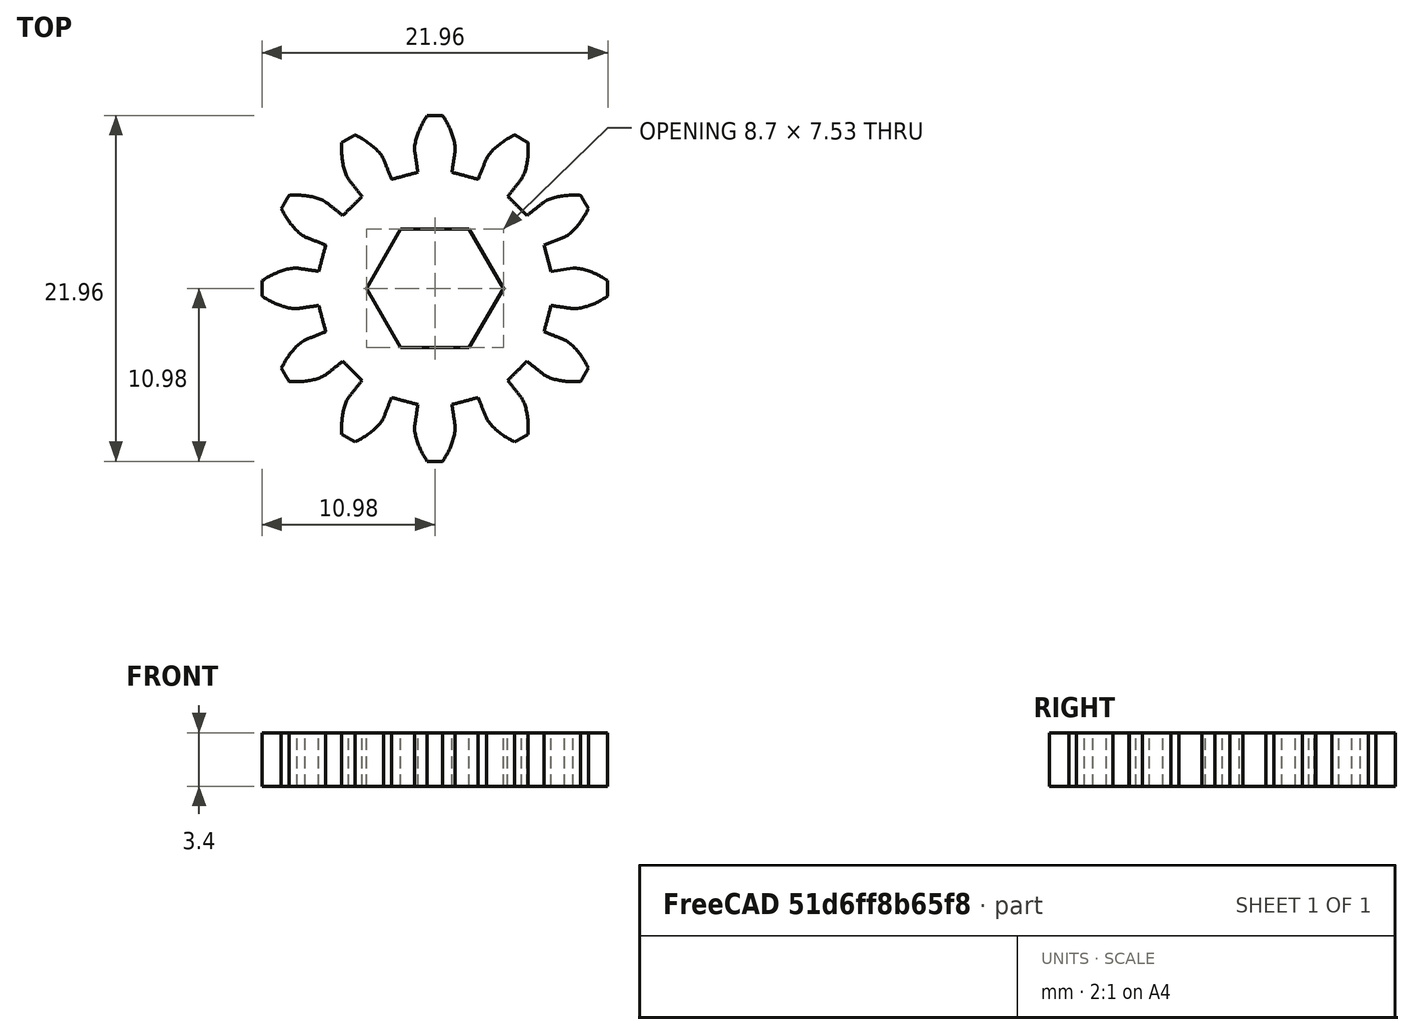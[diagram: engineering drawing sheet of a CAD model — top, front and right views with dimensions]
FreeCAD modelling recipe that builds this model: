
FCSTD DOCUMENT  (FreeCAD 0.20R29603 (Git))
Label: small gear
License: All rights reserved
LicenseURL: http://en.wikipedia.org/wiki/All_rights_reserved
objects: PartDesign::FeaturePython×1, PartDesign::SubtractivePrism×1, PartDesign::Body×1
note: 4 computed .brp shape members not serialized (recipe doc carries the construction recipe); baked Part::Feature solids carry a one-line shape summary decoded from their .brp

FEATURE [PartDesign::FeaturePython] InvoluteGear  # WARN: FeaturePython — macro-defined, semantics opaque (R4)
  AttacherType = Attacher::AttachEngine3D
  angular_backlash = 0
  backlash = 0
  beta = 0
  clearance = 0.25
  da = 21.98
  df = 14.915
  double_helix = false
  dw = 18.84
  head = 0
  head_fillet = 0
  height = 3.4
  module = 1.57
  numpoints = 6
  pressure_angle = 20
  properties_from_tool = false
  reversed_backlash = false
  root_fillet = 0
  shift = 0
  simple = false
  teeth = 12
  transverse_pitch = 4.9323
  traverse_module = 1.57
  undercut = false
  version = 0.0.4
  expr: angular_backlash = backlash / dw * 360° / pi
FEATURE [PartDesign::SubtractivePrism] Prism
  AttacherType = Attacher::AttachEngine3D
  BaseFeature = -> InvoluteGear
  Circumradius = 4.35
  FirstAngle = 0
  Height = 3.4
  Polygon = 6
  Refine = true
  SecondAngle = 0
FEATURE [PartDesign::Body] Body
  Group = -> [InvoluteGear,Prism]
  Origin = -> Origin
  Tip = -> Prism
